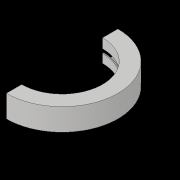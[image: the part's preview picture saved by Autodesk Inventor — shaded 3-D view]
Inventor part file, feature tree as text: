
AUTODESK INVENTOR PART (.ipt)
format: ipt  version: 2017 (Build 210142000, 142)  size: 135,168 bytes
history: native  units: in
note: dims shown in document units (in); Inventor stores cm internally (conversion verified against a paired STEP export)
features: revolve x1, sketch x1
ambient origin geometry x8: Origin, YZ Plane, XZ Plane, XY Plane, X Axis, Y Axis, Z Axis, Center Point
bodies: Solid1 (feature_tree)
feature tree (2):
  revolve  "Revolution1"  [1 undecoded]
  sketch  "Sketch1"  dims[d0=2.0in d2=10.5in d3=2.0in d4=2.875in d5=0.125in d6=0.125in d7=0.125in d8=0.125in d9=0.125in d10=0.125in d11=0.125in d12=0.125in d13=1.0285in d14=0.5in d15=180.0deg d16=5.25in d17=0.125in d18=0.125in]
note: 1 required parameter value undecoded (feature->parameter linkage not recoverable at this tier; creation-order binding heuristic only, values carry confidence <= 0.55)
